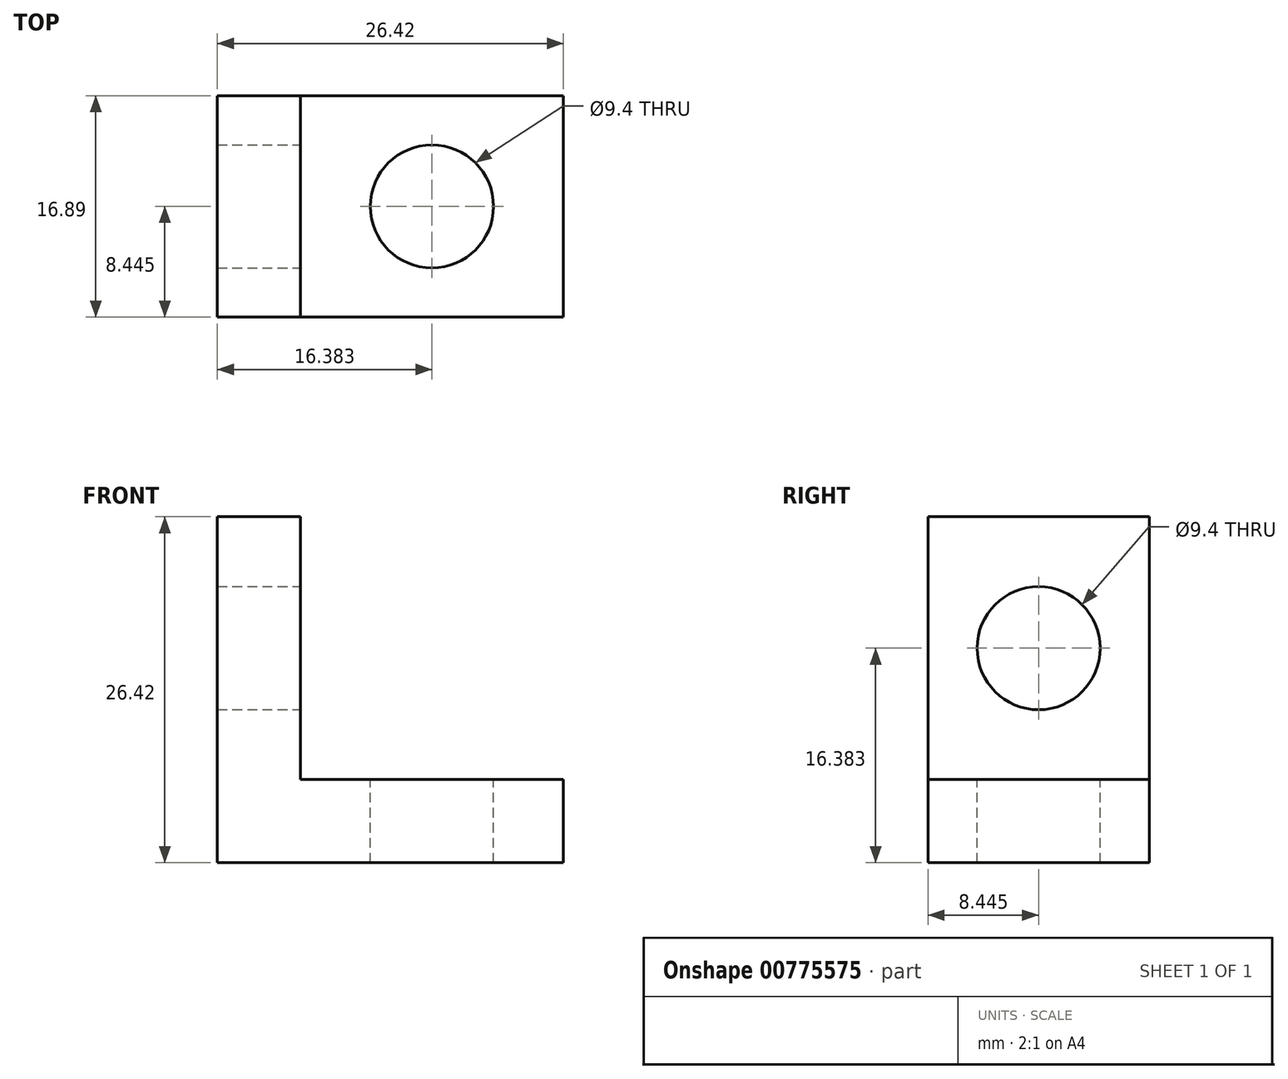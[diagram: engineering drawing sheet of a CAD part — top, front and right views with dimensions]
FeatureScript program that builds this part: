
annotation { "Feature Type Name" : "Feature", "Feature Type Description" : "" }
export const myFeature = defineFeature(function(context is Context, id is Id, definition is map)
    precondition{}
    {
        {
            var Q0;
            Q0=qCreatedBy(makeId("Front.planeOp"),FACE);
            var sketch = newSketch(context, id + "F0", { "sketchPlane" : qUnion([Q0])});
            skLineSegment(sketch, "E0.bottom", {"start": v(0, 0) * mm, "end": v(6.35, 0) * mm});
            skLineSegment(sketch, "E0.top", {"start": v(0, 26.42) * mm, "end": v(6.35, 26.42) * mm});
            skLineSegment(sketch, "E0.left", {"start": v(0, 0) * mm, "end": v(0, 26.42) * mm});
            skLineSegment(sketch, "E0.right", {"start": v(6.35, 6.35) * mm, "end": v(6.35, 26.42) * mm});
            skLineSegment(sketch, "E1.bottom", {"start": v(0, 0) * mm, "end": v(26.42, 0) * mm});
            skLineSegment(sketch, "E1.top", {"start": v(6.35, 6.35) * mm, "end": v(26.42, 6.35) * mm});
            skLineSegment(sketch, "E1.left", {"start": v(0, 0) * mm, "end": v(0, 6.35) * mm});
            skLineSegment(sketch, "E1.right", {"start": v(26.42, 0) * mm, "end": v(26.42, 6.35) * mm});
            skSolve(sketch);
        }
        {
            var Q0;
            Q0 = qSketchRegion(id + "F0", true);
            extrude(context, id + "F1", {"entities" : qUnion([Q0]), "depth" : 13.72 * mm + 3.17 * mm, "offsetDistance" : 25.4 * mm});
        }
        {
            var Q0;
            Q0=makeQuery(id+"F1.opExtrude","SWEPT_FACE",FACE,{"disambiguationData":[OSD([sQuery(id+"F0.wireOp",EDGE,"E0.right")])]});
            var sketch = newSketch(context, id + "F2", { "sketchPlane" : qUnion([Q0])});
            skCircle(sketch, "E2", {"center": v(-8.45, 16.38) * mm, "radius": 4.7 * mm});
            skLineSegment(sketch, "E3", {"start": v(-8.45, 6.35) * mm, "end": v(-8.45, 26.42) * mm});
            skLineSegment(sketch, "E4", {"start": v(-16.9, 16.38) * mm, "end": v(0, 16.38) * mm});
            skSolve(sketch);
        }
        {
            var Q0;
            Q0 = qSketchRegion(id + "F2", true);
            extrude(context, id + "F3", {"entities" : qUnion([Q0]), "operationType" : NewBodyOperationType.REMOVE, "endBound" : BoundingType.UP_TO_NEXT, "oppositeDirection" : true, "depth" : 25.4 * mm, "offsetDistance" : 25.4 * mm});
        }
        {
            var Q0;
            Q0=makeQuery(id+"F1.opExtrude","SWEPT_FACE",FACE,{"disambiguationData":[OSD([sQuery(id+"F0.wireOp",EDGE,"E1.top")])]});
            var sketch = newSketch(context, id + "F4", { "sketchPlane" : qUnion([Q0])});
            skCircle(sketch, "E5", {"center": v(16.38, -8.45) * mm, "radius": 4.7 * mm});
            skLineSegment(sketch, "E6", {"start": v(6.35, -8.45) * mm, "end": v(26.42, -8.45) * mm});
            skLineSegment(sketch, "E7", {"start": v(16.38, -16.9) * mm, "end": v(16.38, 0) * mm});
            skSolve(sketch);
        }
        {
            var Q0;
            Q0 = qSketchRegion(id + "F4", true);
            extrude(context, id + "F5", {"entities" : qUnion([Q0]), "operationType" : NewBodyOperationType.REMOVE, "endBound" : BoundingType.UP_TO_NEXT, "oppositeDirection" : true, "depth" : 25.4 * mm, "offsetDistance" : 25.4 * mm});
        }
    });
